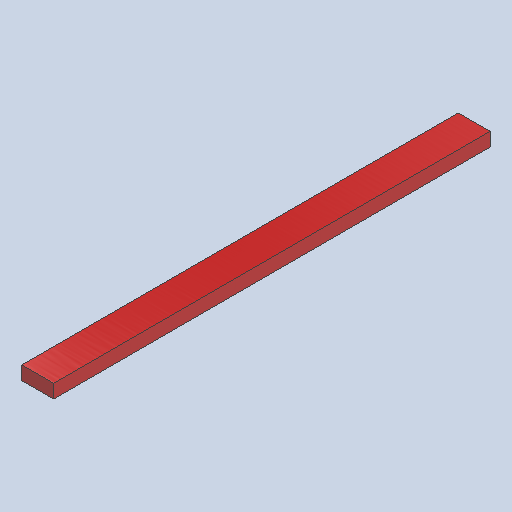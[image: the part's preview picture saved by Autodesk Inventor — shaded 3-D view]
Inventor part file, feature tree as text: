
AUTODESK INVENTOR PART (.ipt)
format: ipt  version: 2025 (Build 290162000, 162)  size: 94,208 bytes
history: native  units: in
note: dims shown in document units (in); Inventor stores cm internally (conversion verified against a paired STEP export)
features: extrude x1, sketch x1, other x1
ambient origin geometry x8: Origin, YZ Plane, XZ Plane, XY Plane, X Axis, Y Axis, Z Axis, Center Point
bodies: Solid1 (feature_tree)
feature tree (3):
  extrude  "Extrusion1"  Depth=3.5in
  sketch  "Sketch1"  dims[d0=1.5in d1=3.5in d2=48.0in d3=0.0in]
  other  "Finish1"
